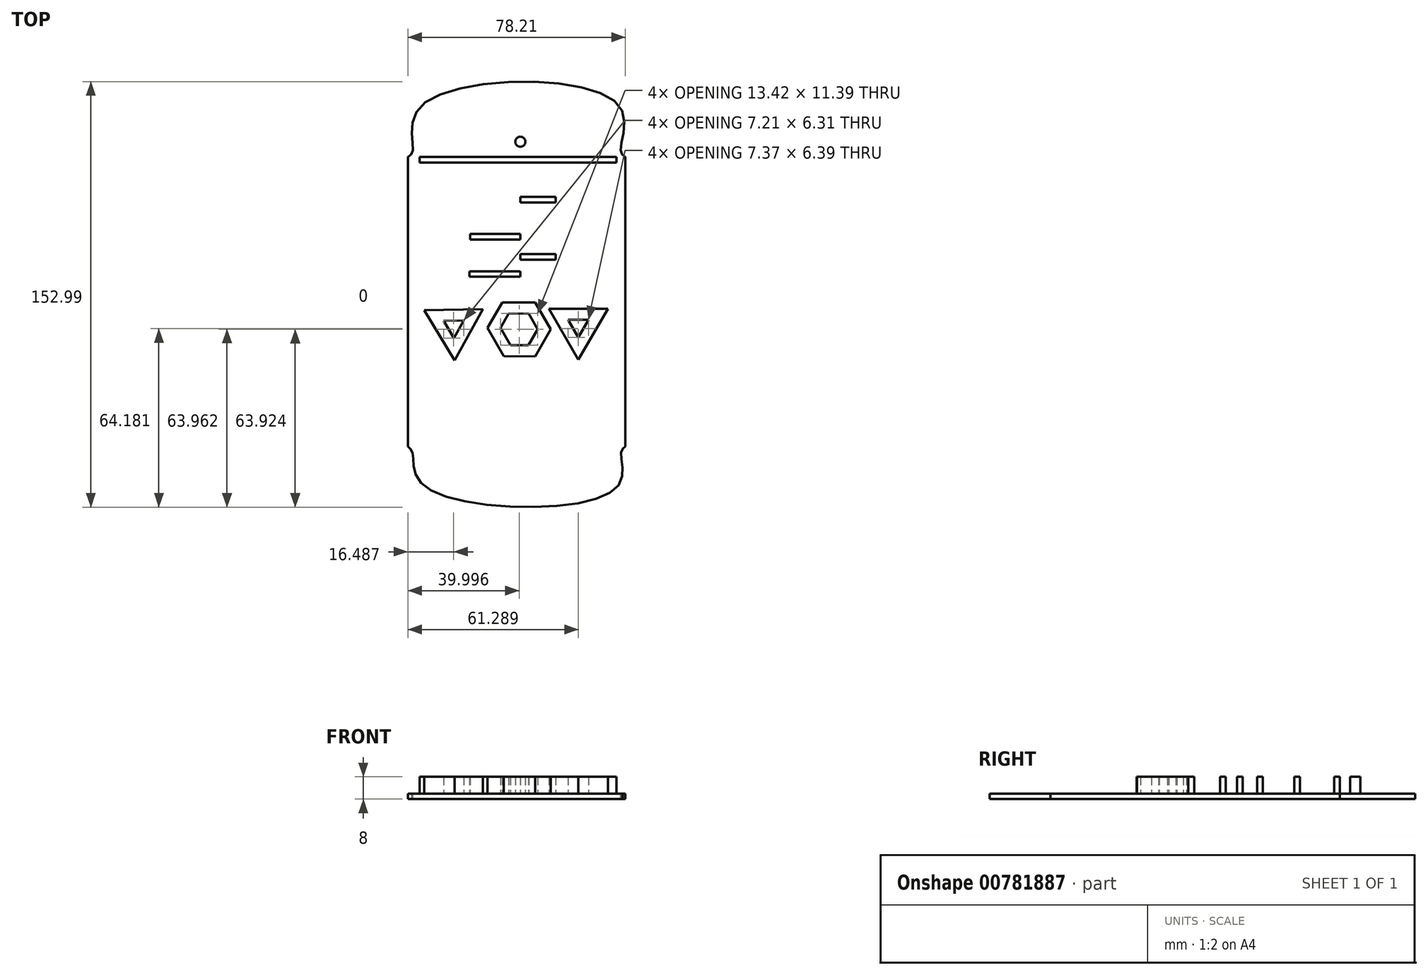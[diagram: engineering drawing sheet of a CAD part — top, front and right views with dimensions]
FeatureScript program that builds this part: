
annotation { "Feature Type Name" : "Feature", "Feature Type Description" : "" }
export const myFeature = defineFeature(function(context is Context, id is Id, definition is map)
    precondition{}
    {
        {
            var Q0;
            Q0=qCreatedBy(makeId("Top.planeOp"),FACE);
            var sketch = newSketch(context, id + "F0", { "sketchPlane" : qUnion([Q0])});
            skPoint(sketch, "E0", {"position": v(-40.43, -53.5) * mm});
            skPoint(sketch, "E1", {"position": v(37.78, -53.5) * mm});
            skLineSegment(sketch, "E2", {"start": v(-32, 50.54) * mm, "end": v(30.05, 50.54) * mm});
            skLineSegment(sketch, "E3", {"start": v(-31.14, -53.5) * mm, "end": v(-2.64, -53.5) * mm});
            skLineSegment(sketch, "E4", {"start": v(-40.43, -53.5) * mm, "end": v(-40.43, 50.54) * mm});
            skLineSegment(sketch, "E5", {"start": v(37.78, 50.54) * mm, "end": v(37.78, -53.5) * mm});
            skPoint(sketch, "E6", {"position": v(-31.01, 62.03) * mm});
            skPoint(sketch, "E7", {"position": v(29.88, 62.03) * mm});
            skFitSpline(sketch, "E8", {"points": [v(-40.43, 50.54) * mm, v(-31.01, 62.03) * mm, v(29.88, 62.03) * mm, v(37.78, 50.54) * mm], "startDerivative": vector(21.62, 30.27) * mm, "endDerivative": vector(21.62, -30.27) * mm});
            skCircle(sketch, "E9", {"center": v(0, 56.08) * mm, "radius": 1.82 * mm});
            skPoint(sketch, "E10", {"position": v(-31.14, -62.43) * mm});
            skFitSpline(sketch, "E11", {"points": [v(-40.43, -53.5) * mm, v(-31.14, -62.43) * mm, v(30.36, -62.47) * mm, v(37.78, -53.5) * mm], "startDerivative": vector(21.38, -31.6) * mm, "endDerivative": vector(20.6, 30.8) * mm});
            skLineSegment(sketch, "E12", {"start": v(-36.19, 50.54) * mm, "end": v(-36.17, 44.53) * mm});
            skLineSegment(sketch, "E13", {"start": v(34.6, 50.54) * mm, "end": v(34.6, 44.68) * mm});
            skLineSegment(sketch, "E14", {"start": v(-35.8, -53.5) * mm, "end": v(-31.14, -53.5) * mm});
            skLineSegment(sketch, "E15", {"start": v(30.05, -53.5) * mm, "end": v(34.6, -53.59) * mm});
            skLineSegment(sketch, "E16", {"start": v(-36.19, 50.54) * mm, "end": v(-32, 50.54) * mm});
            skLineSegment(sketch, "E17", {"start": v(30.05, 50.54) * mm, "end": v(34.6, 50.54) * mm});
            skLineSegment(sketch, "E18", {"start": v(-36.17, 44.53) * mm, "end": v(-2.7, 44.66) * mm});
            skLineSegment(sketch, "E19.0", {"start": v(-36.16, 42.53) * mm, "end": v(-2.81, 42.66) * mm});
            skLineSegment(sketch, "E20", {"start": v(0, 36.24) * mm, "end": v(12.68, 36.24) * mm});
            skLineSegment(sketch, "E21", {"start": v(12.68, 30.32) * mm, "end": v(34.6, 30.32) * mm});
            skLineSegment(sketch, "E22", {"start": v(34.6, 30.32) * mm, "end": v(12.68, 30.32) * mm});
            skLineSegment(sketch, "E23", {"start": v(-36.11, 30.32) * mm, "end": v(-17.98, 30.32) * mm});
            skLineSegment(sketch, "E24", {"start": v(-17.98, 22.86) * mm, "end": v(0, 22.86) * mm});
            skLineSegment(sketch, "E25", {"start": v(0, 15.61) * mm, "end": v(12.68, 15.61) * mm});
            skLineSegment(sketch, "E26", {"start": v(12.68, 9.2) * mm, "end": v(34.6, 9.2) * mm});
            skLineSegment(sketch, "E27", {"start": v(0, 9.48) * mm, "end": v(-18.26, 9.48) * mm});
            skLineSegment(sketch, "E28.0", {"start": v(0, 34.24) * mm, "end": v(12.68, 34.24) * mm});
            skLineSegment(sketch, "E29.0", {"start": v(-36.1, 28.32) * mm, "end": v(-17.98, 28.32) * mm});
            skLineSegment(sketch, "E30.0", {"start": v(12.68, 28.32) * mm, "end": v(34.6, 28.32) * mm});
            skLineSegment(sketch, "E31.0", {"start": v(-17.98, 20.86) * mm, "end": v(0, 20.86) * mm});
            skLineSegment(sketch, "E32.0", {"start": v(0, 13.61) * mm, "end": v(12.68, 13.61) * mm});
            skLineSegment(sketch, "E33.0", {"start": v(0, 7.48) * mm, "end": v(-18.26, 7.48) * mm});
            skLineSegment(sketch, "E34.0", {"start": v(12.68, 7.2) * mm, "end": v(34.6, 7.2) * mm});
            skLineSegment(sketch, "E35", {"start": v(0, 36.24) * mm, "end": v(0, 34.24) * mm});
            skLineSegment(sketch, "E36", {"start": v(12.68, 36.24) * mm, "end": v(12.68, 34.24) * mm});
            skLineSegment(sketch, "E37", {"start": v(12.68, 30.32) * mm, "end": v(12.68, 28.32) * mm});
            skLineSegment(sketch, "E38", {"start": v(0, 22.86) * mm, "end": v(0, 20.86) * mm});
            skLineSegment(sketch, "E39", {"start": v(-17.98, 22.86) * mm, "end": v(-17.98, 20.86) * mm});
            skLineSegment(sketch, "E40", {"start": v(-17.98, 30.32) * mm, "end": v(-17.98, 28.32) * mm});
            skLineSegment(sketch, "E41", {"start": v(0, 15.61) * mm, "end": v(0, 13.61) * mm});
            skLineSegment(sketch, "E42", {"start": v(12.68, 13.61) * mm, "end": v(12.68, 15.61) * mm});
            skLineSegment(sketch, "E43", {"start": v(12.68, 9.2) * mm, "end": v(12.68, 7.2) * mm});
            skLineSegment(sketch, "E44", {"start": v(0, 9.48) * mm, "end": v(0, 7.48) * mm});
            skLineSegment(sketch, "E45", {"start": v(-18.26, 7.48) * mm, "end": v(-18.26, 9.48) * mm});
            skLineSegment(sketch, "E46", {"start": v(2.07, 42.6) * mm, "end": v(2.19, 42.6) * mm});
            skLineSegment(sketch, "E47", {"start": v(2.3, 44.68) * mm, "end": v(34.6, 44.68) * mm});
            skLineSegment(sketch, "E48", {"start": v(2.19, 42.6) * mm, "end": v(34.6, 42.6) * mm});
            skLineSegment(sketch, "E49", {"start": v(-2.7, 44.66) * mm, "end": v(-2.81, 42.66) * mm});
            skLineSegment(sketch, "E50", {"start": v(2.3, 44.68) * mm, "end": v(2.19, 42.6) * mm});
            skFitSpline(sketch, "E51", {"points": [v(-30.8, -28.71) * mm, v(-17.7, -23.7) * mm, v(-6, -28.43) * mm, v(4.88, -23.42) * mm, v(17.98, -28.15) * mm, v(28.12, -24.73) * mm], "startDerivative": vector(63.22, 41.95) * mm, "endDerivative": vector(55.3, 36.27) * mm});
            skFitSpline(sketch, "E52", {"points": [v(-30.8, -28.71) * mm, v(-17.7, -23.7) * mm, v(-6, -28.43) * mm, v(4.88, -23.42) * mm, v(17.98, -28.15) * mm, v(28.85, -24.25) * mm], "startDerivative": vector(63.22, 41.95) * mm, "endDerivative": vector(55.3, 36.27) * mm});
            skLineSegment(sketch, "E53", {"start": v(-30.8, -28.71) * mm, "end": v(-35.9, -28.71) * mm});
            skLineSegment(sketch, "E54.0", {"start": v(-30.8, -30.71) * mm, "end": v(-35.88, -30.71) * mm});
            skFitSpline(sketch, "E55.0", {"points": [v(-29.7, -30.38) * mm, v(-28.38, -29.5) * mm, v(-26.45, -28.23) * mm, v(-24, -26.88) * mm, v(-22.26, -26.11) * mm, v(-20.9, -25.72) * mm, v(-19.88, -25.57) * mm, v(-19.15, -25.53) * mm, v(-18.43, -25.59) * mm, v(-17.74, -25.72) * mm, v(-16.98, -25.96) * mm, v(-15.9, -26.41) * mm, v(-14.46, -27.17) * mm, v(-12.63, -28.25) * mm, v(-11.02, -29.13) * mm, v(-9.65, -29.74) * mm, v(-8.58, -30.12) * mm, v(-7.44, -30.38) * mm, v(-6.44, -30.46) * mm, v(-5.61, -30.42) * mm, v(-4.81, -30.3) * mm, v(-3.86, -30.04) * mm, v(-2.81, -29.6) * mm, v(-1.83, -29.09) * mm, v(-0.9, -28.53) * mm, v(0.29, -27.75) * mm, v(1.69, -26.81) * mm, v(2.99, -26.06) * mm, v(3.94, -25.66) * mm, v(4.5, -25.5) * mm, v(4.91, -25.42) * mm, v(5.3, -25.38) * mm, v(5.85, -25.4) * mm, v(6.58, -25.5) * mm, v(7.64, -25.8) * mm, v(9.12, -26.38) * mm, v(11.03, -27.34) * mm, v(12.7, -28.22) * mm, v(14.08, -28.9) * mm, v(15.13, -29.36) * mm, v(16.22, -29.76) * mm, v(17.15, -30.03) * mm, v(17.91, -30.18) * mm, v(18.67, -30.29) * mm, v(19.61, -30.33) * mm, v(20.71, -30.26) * mm, v(22.13, -30.02) * mm, v(23.8, -29.5) * mm, v(25.68, -28.6) * mm, v(27.47, -27.54) * mm, v(28.64, -26.78) * mm, v(29.22, -26.4) * mm]});
            skFitSpline(sketch, "E55.1", {"points": [v(-29.7, -30.38) * mm, v(-28.38, -29.5) * mm, v(-26.45, -28.23) * mm, v(-24, -26.88) * mm, v(-22.26, -26.11) * mm, v(-20.9, -25.72) * mm, v(-19.88, -25.57) * mm, v(-19.15, -25.53) * mm, v(-18.43, -25.59) * mm, v(-17.74, -25.72) * mm, v(-16.98, -25.96) * mm, v(-15.9, -26.41) * mm, v(-14.46, -27.17) * mm, v(-12.63, -28.25) * mm, v(-11.02, -29.13) * mm, v(-9.65, -29.74) * mm, v(-8.58, -30.12) * mm, v(-7.44, -30.38) * mm, v(-6.44, -30.46) * mm, v(-5.61, -30.42) * mm, v(-4.81, -30.3) * mm, v(-3.86, -30.04) * mm, v(-2.81, -29.6) * mm, v(-1.83, -29.09) * mm, v(-0.9, -28.53) * mm, v(0.29, -27.75) * mm, v(1.69, -26.81) * mm, v(2.99, -26.06) * mm, v(3.94, -25.66) * mm, v(4.5, -25.5) * mm, v(4.91, -25.42) * mm, v(5.3, -25.38) * mm, v(5.85, -25.4) * mm, v(6.58, -25.5) * mm, v(7.64, -25.8) * mm, v(9.12, -26.38) * mm, v(11.03, -27.34) * mm, v(12.7, -28.22) * mm, v(14.08, -28.9) * mm, v(15.13, -29.36) * mm, v(16.22, -29.76) * mm, v(17.15, -30.03) * mm, v(17.91, -30.18) * mm, v(18.67, -30.29) * mm, v(19.61, -30.33) * mm, v(20.71, -30.26) * mm, v(22.13, -30.02) * mm, v(23.8, -29.5) * mm, v(25.68, -28.6) * mm, v(27.47, -27.54) * mm, v(28.64, -26.78) * mm, v(29.22, -26.4) * mm]});
            skFitSpline(sketch, "E55.2", {"points": [v(-29.7, -30.38) * mm, v(-28.38, -29.5) * mm, v(-26.45, -28.23) * mm, v(-24, -26.88) * mm, v(-22.26, -26.11) * mm, v(-20.9, -25.72) * mm, v(-19.88, -25.57) * mm, v(-19.15, -25.53) * mm, v(-18.43, -25.59) * mm, v(-17.74, -25.72) * mm, v(-16.98, -25.96) * mm, v(-15.9, -26.41) * mm, v(-14.46, -27.17) * mm, v(-12.63, -28.25) * mm, v(-11.02, -29.13) * mm, v(-9.65, -29.74) * mm, v(-8.58, -30.12) * mm, v(-7.44, -30.38) * mm, v(-6.44, -30.46) * mm, v(-5.61, -30.42) * mm, v(-4.81, -30.3) * mm, v(-3.86, -30.04) * mm, v(-2.81, -29.6) * mm, v(-1.83, -29.09) * mm, v(-0.9, -28.53) * mm, v(0.29, -27.75) * mm, v(1.69, -26.81) * mm, v(2.99, -26.06) * mm, v(3.94, -25.66) * mm, v(4.5, -25.5) * mm, v(4.91, -25.42) * mm, v(5.3, -25.38) * mm, v(5.85, -25.4) * mm, v(6.58, -25.5) * mm, v(7.64, -25.8) * mm, v(9.12, -26.38) * mm, v(11.03, -27.34) * mm, v(12.7, -28.22) * mm, v(14.08, -28.9) * mm, v(15.13, -29.36) * mm, v(16.22, -29.76) * mm, v(17.15, -30.03) * mm, v(17.91, -30.18) * mm, v(18.67, -30.29) * mm, v(19.61, -30.33) * mm, v(20.71, -30.26) * mm, v(22.13, -30.02) * mm, v(23.8, -29.5) * mm, v(25.68, -28.6) * mm, v(27.47, -27.54) * mm, v(28.64, -26.78) * mm, v(29.22, -26.4) * mm]});
            skLineSegment(sketch, "E56", {"start": v(-30.8, -30.71) * mm, "end": v(-29.7, -30.38) * mm});
            skArc(sketch, "E57", {"start": v(0.85, -27.38) * mm, "mid": v(0.96, -26.1) * mm, "end": v(-0.25, -25.7) * mm});
            skFitSpline(sketch, "E58.1", {"points": [v(-29.7, -30.38) * mm, v(-28.38, -29.5) * mm, v(-26.44, -28.22) * mm, v(-23.99, -26.87) * mm, v(-22.23, -26.1) * mm, v(-20.86, -25.7) * mm, v(-19.83, -25.56) * mm, v(-19.08, -25.54) * mm, v(-18.49, -25.59) * mm, v(-18.02, -25.67) * mm, v(-17.53, -25.78) * mm, v(-16.89, -26) * mm, v(-15.8, -26.46) * mm, v(-14.34, -27.24) * mm, v(-12.5, -28.33) * mm, v(-10.86, -29.21) * mm, v(-9.48, -29.81) * mm, v(-8.4, -30.18) * mm, v(-7.43, -30.37) * mm, v(-6.62, -30.45) * mm, v(-6, -30.45) * mm, v(-5.38, -30.39) * mm, v(-4.58, -30.25) * mm, v(-3.64, -29.96) * mm, v(-2.6, -29.5) * mm, v(-1.3, -28.79) * mm, v(0.21, -27.8) * mm, v(1.62, -26.86) * mm, v(2.67, -26.24) * mm, v(3.43, -25.86) * mm, v(4.13, -25.6) * mm, v(4.77, -25.43) * mm, v(5.36, -25.38) * mm, v(6.02, -25.42) * mm, v(6.77, -25.57) * mm, v(7.85, -25.9) * mm, v(9.35, -26.55) * mm, v(11.29, -27.55) * mm, v(13, -28.44) * mm, v(14.41, -29.1) * mm, v(15.5, -29.55) * mm, v(16.45, -29.86) * mm, v(17.22, -30.05) * mm, v(18.02, -30.2) * mm, v(19, -30.3) * mm, v(20.16, -30.27) * mm, v(21.28, -30.13) * mm, v(22.73, -29.8) * mm, v(24.45, -29.16) * mm, v(26.37, -28.18) * mm, v(28.2, -27.07) * mm, v(29.37, -26.3) * mm, v(29.95, -25.92) * mm]});
            skArc(sketch, "E59", {"start": v(4.88, -23.42) * mm, "mid": v(4.71, -24.43) * mm, "end": v(5.06, -25.4) * mm});
            skLineSegment(sketch, "E60.bottom", {"start": v(-33.47, -33.75) * mm, "end": v(-2.31, -33.75) * mm});
            skLineSegment(sketch, "E60.top", {"start": v(-33.47, -36.42) * mm, "end": v(-2.31, -36.42) * mm});
            skLineSegment(sketch, "E61", {"start": v(2.25, -33.75) * mm, "end": v(31.53, -33.75) * mm});
            skLineSegment(sketch, "E62", {"start": v(2.25, -36.42) * mm, "end": v(31.53, -36.42) * mm});
            skLineSegment(sketch, "E63", {"start": v(-2.31, -33.75) * mm, "end": v(-2.31, -36.42) * mm});
            skLineSegment(sketch, "E64", {"start": v(2.25, -33.75) * mm, "end": v(2.25, -36.42) * mm});
            skLineSegment(sketch, "E65", {"start": v(-33.47, -33.75) * mm, "end": v(-35.87, -33.75) * mm});
            skLineSegment(sketch, "E66", {"start": v(-35.86, -36.42) * mm, "end": v(-33.47, -36.42) * mm});
            skLineSegment(sketch, "E67", {"start": v(31.53, -33.75) * mm, "end": v(34.6, -33.75) * mm});
            skLineSegment(sketch, "E68", {"start": v(31.53, -36.42) * mm, "end": v(34.6, -36.42) * mm});
            skFitSpline(sketch, "E69", {"points": [v(-35.83, -46) * mm, v(-2.69, -45.92) * mm, v(1.31, -45.92) * mm, v(34.6, -46.48) * mm], "startDerivative": vector(98.58, 0.2) * mm, "endDerivative": vector(96.45, -1.3) * mm});
            skFitSpline(sketch, "E70.0", {"points": [v(-35.82, -48) * mm, v(-33.77, -48) * mm, v(-29.65, -47.98) * mm, v(-23.62, -47.97) * mm, v(-17.92, -47.96) * mm, v(-12.73, -47.95) * mm, v(-9, -47.94) * mm, v(-6.44, -47.93) * mm, v(-4.76, -47.93) * mm, v(-3.6, -47.92) * mm, v(-2.8, -47.92) * mm, v(-2.1, -47.91) * mm, v(-1.4, -47.9) * mm, v(-0.68, -47.9) * mm, v(0.03, -47.9) * mm, v(0.74, -47.91) * mm, v(1.44, -47.92) * mm, v(2.25, -47.93) * mm, v(3.44, -47.95) * mm, v(5.15, -47.98) * mm, v(7.74, -48.02) * mm, v(11.54, -48.1) * mm, v(16.78, -48.2) * mm, v(22.5, -48.3) * mm, v(28.5, -48.4) * mm, v(32.56, -48.45) * mm, v(34.57, -48.48) * mm]});
            skFitSpline(sketch, "E71.0", {"points": [v(-35.82, -48) * mm, v(-33.77, -48) * mm, v(-29.65, -47.98) * mm, v(-23.62, -47.97) * mm, v(-17.92, -47.96) * mm, v(-12.73, -47.95) * mm, v(-9, -47.94) * mm, v(-6.44, -47.93) * mm, v(-4.76, -47.93) * mm, v(-3.6, -47.92) * mm, v(-2.8, -47.92) * mm, v(-2.1, -47.91) * mm, v(-1.4, -47.9) * mm, v(-0.68, -47.9) * mm, v(0.03, -47.9) * mm, v(0.74, -47.91) * mm, v(1.44, -47.92) * mm, v(2.25, -47.93) * mm, v(3.44, -47.95) * mm, v(5.15, -47.98) * mm, v(7.74, -48.02) * mm, v(11.54, -48.1) * mm, v(16.78, -48.2) * mm, v(22.5, -48.3) * mm, v(28.5, -48.4) * mm, v(32.56, -48.45) * mm, v(34.57, -48.48) * mm]});
            skLineSegment(sketch, "E72", {"start": v(-2.64, -47.92) * mm, "end": v(-2.69, -45.92) * mm});
            skLineSegment(sketch, "E73", {"start": v(1.31, -45.92) * mm, "end": v(1.36, -47.92) * mm});
            skPoint(sketch, "E74", {"position": v(-2.64, -53.5) * mm});
            skPoint(sketch, "E75", {"position": v(1.36, -53.5) * mm});
            skLineSegment(sketch, "E76.trimOffspring", {"start": v(1.36, -53.5) * mm, "end": v(30.05, -53.5) * mm});
            skLineSegment(sketch, "E77", {"start": v(-2.64, -53.5) * mm, "end": v(-4.77, -64.81) * mm});
            skLineSegment(sketch, "E78", {"start": v(1.36, -53.5) * mm, "end": v(5.18, -64.86) * mm});
            skLineSegment(sketch, "E79", {"start": v(5.18, -64.86) * mm, "end": v(1.36, -53.5) * mm});
            skLineSegment(sketch, "E80.trimOffspring", {"start": v(34.6, 7.2) * mm, "end": v(34.6, -24.25) * mm});
            skLineSegment(sketch, "E81.trimOffspring", {"start": v(-35.86, -36.42) * mm, "end": v(-35.83, -46) * mm});
            skLineSegment(sketch, "E82.trimOffspring", {"start": v(34.6, -36.42) * mm, "end": v(34.6, -46.48) * mm});
            skLineSegment(sketch, "E83.trimOffspring", {"start": v(-35.88, -30.71) * mm, "end": v(-35.87, -33.75) * mm});
            skLineSegment(sketch, "E84.trimOffspring", {"start": v(34.6, 28.32) * mm, "end": v(34.6, 9.2) * mm});
            skLineSegment(sketch, "E85.trimOffspring", {"start": v(34.6, 42.6) * mm, "end": v(34.6, 30.32) * mm});
            skLineSegment(sketch, "E86.trimOffspring", {"start": v(-36.16, 42.53) * mm, "end": v(-36.11, 30.32) * mm});
            skLineSegment(sketch, "E87.trimOffspring", {"start": v(-36.1, 28.32) * mm, "end": v(-35.9, -28.71) * mm});
            skLineSegment(sketch, "E88", {"start": v(28.85, -24.25) * mm, "end": v(34.6, -24.25) * mm});
            skLineSegment(sketch, "E89", {"start": v(28.71, -26.73) * mm, "end": v(34.6, -26.73) * mm});
            skLineSegment(sketch, "E90", {"start": v(28.12, -24.73) * mm, "end": v(28.85, -24.25) * mm});
            skLineSegment(sketch, "E91.trimOffspring", {"start": v(34.6, -26.73) * mm, "end": v(34.6, -33.75) * mm});
            skLineSegment(sketch, "E92.0", {"start": v(10.9, -11.44) * mm, "end": v(5.29, -21.11) * mm});
            skLineSegment(sketch, "E92.1", {"start": v(5.29, -21.11) * mm, "end": v(-5.9, -21.1) * mm});
            skLineSegment(sketch, "E92.2", {"start": v(-5.9, -21.1) * mm, "end": v(-11.76, -10.9) * mm});
            skLineSegment(sketch, "E92.3", {"start": v(-11.76, -10.9) * mm, "end": v(-6.44, -1.72) * mm});
            skLineSegment(sketch, "E92.4", {"start": v(-6.44, -1.72) * mm, "end": v(5.32, -1.74) * mm});
            skLineSegment(sketch, "E92.5", {"start": v(5.32, -1.74) * mm, "end": v(10.9, -11.44) * mm});
            skPoint(sketch, "E92.0.midPoint", {"position": v(8.1, -16.27) * mm});
            skLineSegment(sketch, "E93.0", {"start": v(-7.14, -10.9) * mm, "end": v(-4.14, -5.72) * mm});
            skLineSegment(sketch, "E93.1", {"start": v(3, -5.74) * mm, "end": v(6.28, -11.43) * mm});
            skLineSegment(sketch, "E93.2", {"start": v(6.28, -11.43) * mm, "end": v(2.98, -17.1) * mm});
            skLineSegment(sketch, "E93.3", {"start": v(-4.14, -5.72) * mm, "end": v(3, -5.74) * mm});
            skLineSegment(sketch, "E93.4", {"start": v(2.98, -17.1) * mm, "end": v(-3.58, -17.1) * mm});
            skLineSegment(sketch, "E93.5", {"start": v(-3.58, -17.1) * mm, "end": v(-7.14, -10.9) * mm});
            skLineSegment(sketch, "E94.0", {"start": v(-13.5, -4.08) * mm, "end": v(-23.66, -22.53) * mm});
            skLineSegment(sketch, "E94.1", {"start": v(-23.66, -22.53) * mm, "end": v(-34.55, -4.5) * mm});
            skLineSegment(sketch, "E94.2", {"start": v(-34.55, -4.5) * mm, "end": v(-13.5, -4.08) * mm});
            skPoint(sketch, "E94.0.midPoint", {"position": v(-18.58, -13.3) * mm});
            skLineSegment(sketch, "E95.0", {"start": v(-27.55, -8.37) * mm, "end": v(-20.34, -8.22) * mm});
            skLineSegment(sketch, "E95.1", {"start": v(-23.82, -14.53) * mm, "end": v(-27.55, -8.37) * mm});
            skLineSegment(sketch, "E95.2", {"start": v(-20.34, -8.22) * mm, "end": v(-23.82, -14.53) * mm});
            skLineSegment(sketch, "E96.0", {"start": v(31.47, -3.96) * mm, "end": v(20.88, -22.35) * mm});
            skLineSegment(sketch, "E96.1", {"start": v(20.88, -22.35) * mm, "end": v(10.24, -3.99) * mm});
            skLineSegment(sketch, "E96.2", {"start": v(10.24, -3.99) * mm, "end": v(31.47, -3.96) * mm});
            skPoint(sketch, "E96.0.midPoint", {"position": v(26.17, -13.15) * mm});
            skLineSegment(sketch, "E97.0", {"start": v(17.17, -7.98) * mm, "end": v(24.54, -7.97) * mm});
            skLineSegment(sketch, "E97.1", {"start": v(20.87, -14.35) * mm, "end": v(17.17, -7.98) * mm});
            skLineSegment(sketch, "E97.2", {"start": v(24.54, -7.97) * mm, "end": v(20.87, -14.35) * mm});
            skLineSegment(sketch, "E98", {"start": v(-35.82, -48) * mm, "end": v(-35.8, -53.5) * mm});
            skLineSegment(sketch, "E99", {"start": v(34.38, -48.48) * mm, "end": v(34.6, -53.59) * mm});
            skLineSegment(sketch, "E100.0", {"start": v(-5.05, -55.5) * mm, "end": v(-6.8, -64.72) * mm});
            skLineSegment(sketch, "E100.1", {"start": v(-31.14, -55.5) * mm, "end": v(-5.05, -55.5) * mm});
            skLineSegment(sketch, "E100.2", {"start": v(-35.83, -55.5) * mm, "end": v(-31.14, -55.5) * mm});
            skLineSegment(sketch, "E101.0", {"start": v(30.14, -55.41) * mm, "end": v(34.42, -55.58) * mm});
            skLineSegment(sketch, "E101.1", {"start": v(4.03, -55.41) * mm, "end": v(30.14, -55.41) * mm});
            skFitSpline(sketch, "E102.0", {"points": [v(-38.8, 49.38) * mm, v(-38.5, 49.79) * mm, v(-38, 50.64) * mm, v(-37.33, 51.98) * mm, v(-36.63, 53.38) * mm, v(-35.83, 54.8) * mm, v(-34.86, 56.23) * mm, v(-33.64, 57.64) * mm, v(-32.36, 58.77) * mm, v(-31.13, 59.64) * mm, v(-30.1, 60.26) * mm, v(-28.93, 60.86) * mm, v(-27.19, 61.63) * mm, v(-24.7, 62.51) * mm, v(-21.31, 63.43) * mm, v(-16.34, 64.44) * mm, v(-9.45, 65.32) * mm, v(-0.67, 65.72) * mm, v(8.1, 65.45) * mm, v(16.29, 64.51) * mm, v(22.19, 63.17) * mm, v(26.05, 61.8) * mm, v(28.04, 60.83) * mm, v(29.33, 60.01) * mm, v(30.46, 59.16) * mm, v(31.6, 58.03) * mm, v(32.66, 56.6) * mm, v(33.48, 55.14) * mm, v(34.14, 53.65) * mm, v(34.73, 52.18) * mm, v(35.33, 50.75) * mm, v(35.83, 49.82) * mm, v(36.15, 49.38) * mm]});
            skFitSpline(sketch, "E103.0", {"points": [v(-38.8, 49.38) * mm, v(-38.5, 49.79) * mm, v(-38, 50.64) * mm, v(-37.33, 51.98) * mm, v(-36.63, 53.38) * mm, v(-35.83, 54.8) * mm, v(-34.86, 56.23) * mm, v(-33.64, 57.64) * mm, v(-32.36, 58.77) * mm, v(-31.13, 59.64) * mm, v(-30.1, 60.26) * mm, v(-28.93, 60.86) * mm, v(-27.19, 61.63) * mm, v(-24.7, 62.51) * mm, v(-21.31, 63.43) * mm, v(-16.34, 64.44) * mm, v(-9.45, 65.32) * mm, v(-0.67, 65.72) * mm, v(8.1, 65.45) * mm, v(16.29, 64.51) * mm, v(22.19, 63.17) * mm, v(26.05, 61.8) * mm, v(28.04, 60.83) * mm, v(29.33, 60.01) * mm, v(30.46, 59.16) * mm, v(31.6, 58.03) * mm, v(32.66, 56.6) * mm, v(33.48, 55.14) * mm, v(34.14, 53.65) * mm, v(34.73, 52.18) * mm, v(35.33, 50.75) * mm, v(35.83, 49.82) * mm, v(36.15, 49.38) * mm]});
            skCircle(sketch, "E104.0", {"center": v(0, 56.08) * mm, "radius": 3.82 * mm});
            skLineSegment(sketch, "E105", {"start": v(-4.77, -64.81) * mm, "end": v(-2.64, -53.5) * mm});
            skPoint(sketch, "E106.start.orphan", {"position": v(-5.15, -66.8) * mm});
            skPoint(sketch, "E107.orphan", {"position": v(5.85, -66.84) * mm});
            skLineSegment(sketch, "E108", {"start": v(34.6, 50.54) * mm, "end": v(35.46, 50.54) * mm});
            skPoint(sketch, "E109.endSnap0", {"position": v(-37.31, 50.02) * mm});
            skFitSpline(sketch, "E110", {"points": [v(-38.8, 49.38) * mm, v(-38.5, 49.79) * mm, v(-38, 50.64) * mm, v(-37.33, 51.98) * mm, v(-36.63, 53.38) * mm, v(-35.83, 54.8) * mm, v(-34.86, 56.23) * mm, v(-33.64, 57.64) * mm, v(-32.36, 58.77) * mm, v(-31.13, 59.64) * mm, v(-30.1, 60.26) * mm, v(-28.93, 60.86) * mm, v(-27.19, 61.63) * mm, v(-24.7, 62.51) * mm, v(-21.31, 63.43) * mm, v(-16.34, 64.44) * mm, v(-9.45, 65.32) * mm, v(-0.67, 65.72) * mm, v(8.1, 65.45) * mm, v(16.29, 64.51) * mm, v(22.19, 63.17) * mm, v(26.05, 61.8) * mm, v(28.04, 60.83) * mm, v(29.33, 60.01) * mm, v(30.46, 59.16) * mm, v(31.6, 58.03) * mm, v(32.66, 56.6) * mm, v(33.48, 55.14) * mm, v(34.14, 53.65) * mm, v(34.73, 52.18) * mm, v(35.33, 50.75) * mm, v(35.83, 49.82) * mm, v(36.15, 49.38) * mm]});
            skLineSegment(sketch, "E111", {"start": v(-38.08, 50.54) * mm, "end": v(-36.19, 50.54) * mm});
            skLineSegment(sketch, "E112.0", {"start": v(30.05, 48.54) * mm, "end": v(34.24, 48.54) * mm});
            skLineSegment(sketch, "E112.1", {"start": v(-32, 48.54) * mm, "end": v(30.05, 48.54) * mm});
            skLineSegment(sketch, "E112.2", {"start": v(-36.19, 48.54) * mm, "end": v(-32, 48.54) * mm});
            skLineSegment(sketch, "E113", {"start": v(34.24, 48.54) * mm, "end": v(34.6, 48.54) * mm});
            skLineSegment(sketch, "E114", {"start": v(7.18, -64.76) * mm, "end": v(4.03, -55.41) * mm});
            skFitSpline(sketch, "E115.0", {"points": [v(-38.77, -52.37) * mm, v(-38.52, -52.74) * mm, v(-38.06, -53.5) * mm, v(-37.16, -54.98) * mm, v(-36.17, -56.43) * mm, v(-34.8, -57.84) * mm, v(-33.53, -58.88) * mm, v(-31.9, -59.9) * mm, v(-29.85, -60.84) * mm, v(-27.27, -61.73) * mm, v(-23.25, -62.79) * mm, v(-17.3, -63.85) * mm, v(-9.2, -64.66) * mm, v(-0.64, -65) * mm, v(7.9, -64.84) * mm, v(14.6, -64.29) * mm, v(19.45, -63.6) * mm, v(22.78, -62.95) * mm, v(25.24, -62.31) * mm, v(26.97, -61.75) * mm, v(28.15, -61.3) * mm, v(29.2, -60.83) * mm, v(30.4, -60.19) * mm, v(31.6, -59.34) * mm, v(32.68, -58.28) * mm, v(33.8, -56.8) * mm, v(34.6, -55.24) * mm, v(35.38, -53.61) * mm, v(35.84, -52.79) * mm, v(36.12, -52.38) * mm]});
            skLineSegment(sketch, "E116", {"start": v(-36.78, -55.5) * mm, "end": v(-35.83, -55.5) * mm});
            skLineSegment(sketch, "E117", {"start": v(7.18, -64.76) * mm, "end": v(7.18, -64.79) * mm});
            skSolve(sketch);
        }
        {
            var Q0;
            Q0=makeQuery(id+"F0.imprint","IMPRINT",FACE,{"disambiguationData":[TD([[makeQuery(id+"F0.imprint","IMPRINT",EDGE,{"derivedFrom":sQuery(id+"F0.wireOp",EDGE,"E20")}),-1.0]])]});
            var Q1;
            Q1=makeQuery(id+"F0.imprint","IMPRINT",FACE,{"disambiguationData":[TD([[makeQuery(id+"F0.imprint","IMPRINT",EDGE,{"derivedFrom":sQuery(id+"F0.wireOp",EDGE,"E24")}),-1.0]])]});
            var Q2;
            Q2=makeQuery(id+"F0.imprint","IMPRINT",FACE,{"disambiguationData":[TD([[makeQuery(id+"F0.imprint","IMPRINT",EDGE,{"derivedFrom":sQuery(id+"F0.wireOp",EDGE,"E25")}),-1.0]])]});
            var Q3;
            Q3=makeQuery(id+"F0.imprint","IMPRINT",FACE,{"disambiguationData":[TD([[makeQuery(id+"F0.imprint","IMPRINT",EDGE,{"derivedFrom":sQuery(id+"F0.wireOp",EDGE,"E27")}),1.0]])]});
            var Q4;
            Q4=makeQuery(id+"F0.imprint","IMPRINT",FACE,{"disambiguationData":[TD([[makeQuery(id+"F0.imprint","IMPRINT",EDGE,{"derivedFrom":sQuery(id+"F0.wireOp",EDGE,"E94.0")}),-1.0]])]});
            var Q5;
            Q5=makeQuery(id+"F0.imprint","IMPRINT",FACE,{"disambiguationData":[TD([[makeQuery(id+"F0.imprint","IMPRINT",EDGE,{"derivedFrom":sQuery(id+"F0.wireOp",EDGE,"E92.0")}),-1.0]])]});
            var Q6;
            Q6=makeQuery(id+"F0.imprint","IMPRINT",FACE,{"disambiguationData":[TD([[makeQuery(id+"F0.imprint","IMPRINT",EDGE,{"derivedFrom":sQuery(id+"F0.wireOp",EDGE,"E96.0")}),-1.0]])]});
            var Q7;
            Q7=makeQuery(id+"F0.imprint","IMPRINT",FACE,{"disambiguationData":[TD([[makeQuery(id+"F0.imprint","IMPRINT",EDGE,{"derivedFrom":sQuery(id+"F0.wireOp",EDGE,"E9")}),1.0]])]});
            var Q8;
            Q8=makeQuery(id+"F0.imprint","IMPRINT",FACE,{"disambiguationData":[TD([[makeQuery(id+"F0.imprint","IMPRINT",EDGE,{"derivedFrom":sQuery(id+"F0.wireOp",EDGE,"E2")}),-1.0]])]});
            var Q9;
            Q9=makeQuery(id+"F0.imprint","IMPRINT",FACE,{"disambiguationData":[TD([[makeQuery(id+"F0.imprint","IMPRINT",EDGE,{"derivedFrom":sQuery(id+"F0.wireOp",EDGE,"E3")}),-1.0]])]});
            extrude(context, id + "F1", {"entities" : qUnion([Q0, Q1, Q2, Q3, Q4, Q5, Q6, Q7, Q8, Q9]), "depth" : 6 * mm, "offsetDistance" : 25 * mm});
        }
        {
            var Q0;
            Q0=qCreatedBy(makeId("Top.planeOp"),FACE);
            var sketch = newSketch(context, id + "F2", { "sketchPlane" : qUnion([Q0])});
            skLineSegment(sketch, "E118.0", {"start": v(37.78, 50.54) * mm, "end": v(37.78, -53.5) * mm});
            skLineSegment(sketch, "E119.0", {"start": v(-40.43, -53.5) * mm, "end": v(-40.43, 50.54) * mm});
            skFitSpline(sketch, "E120.0", {"points": [v(-40.43, 50.54) * mm, v(-38.62, 53.06) * mm, v(-35.37, 69.23) * mm, v(34.86, 69.72) * mm, v(36.03, 52.99) * mm, v(37.78, 50.54) * mm]});
            skFitSpline(sketch, "E121.0", {"points": [v(-40.43, -53.5) * mm, v(-38.7, -56.04) * mm, v(-34.21, -67.99) * mm, v(34.1, -68.83) * mm, v(36.2, -55.85) * mm, v(37.78, -53.5) * mm]});
            skSolve(sketch);
        }
        {
            var Q0;
            Q0 = qSketchRegion(id + "F2", true);
            extrude(context, id + "F3", {"entities" : qUnion([Q0]), "oppositeDirection" : true, "depth" : 2 * mm, "offsetDistance" : 25 * mm});
        }
    });
